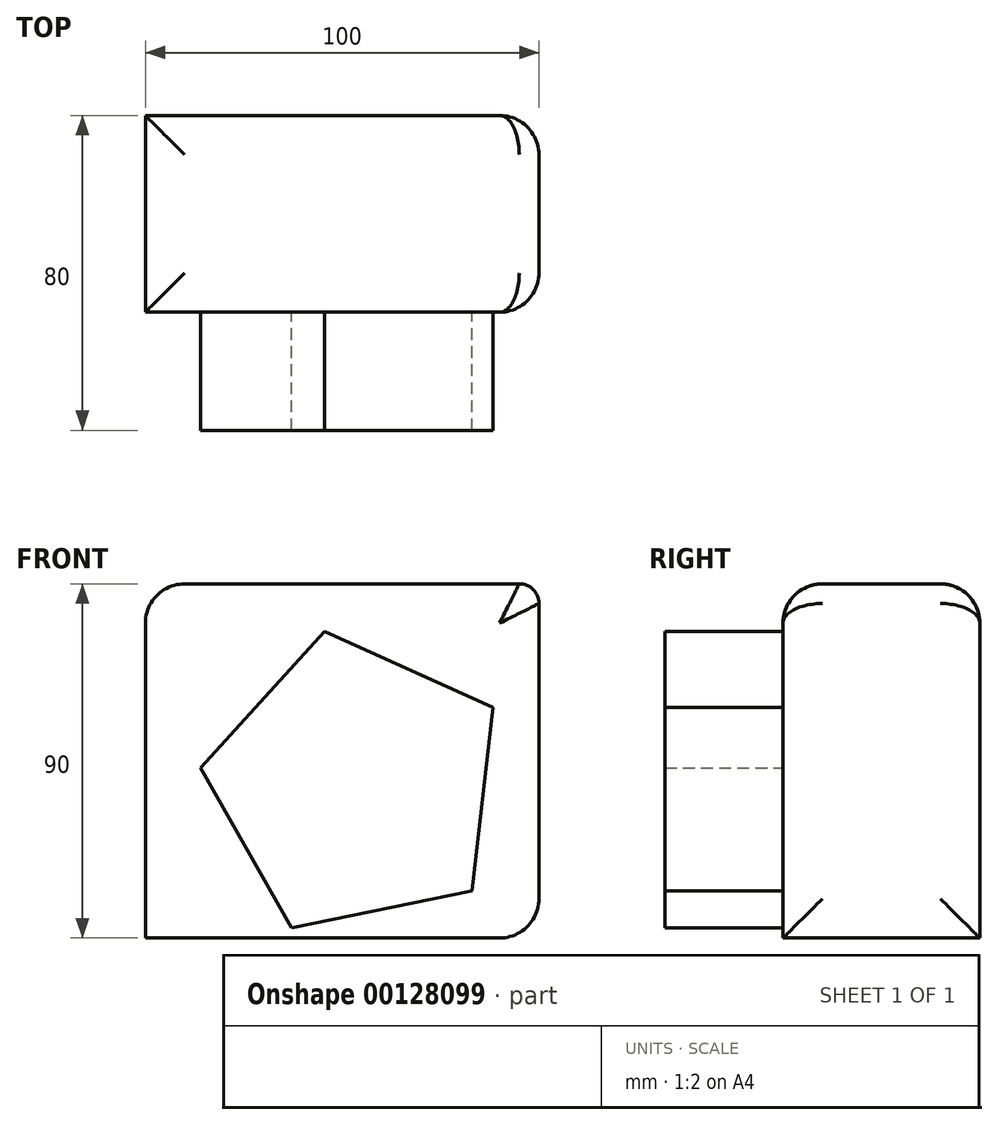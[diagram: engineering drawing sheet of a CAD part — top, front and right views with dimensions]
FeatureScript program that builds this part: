
annotation { "Feature Type Name" : "Feature", "Feature Type Description" : "" }
export const myFeature = defineFeature(function(context is Context, id is Id, definition is map)
    precondition{}
    {
        {
            var Q0;
            Q0=qCreatedBy(makeId("Front.planeOp"),FACE);
            var sketch = newSketch(context, id + "F0", { "sketchPlane" : qUnion([Q0])});
            skLineSegment(sketch, "E0.bottom", {"start": v(-53.61, 60) * mm, "end": v(46.39, 60) * mm});
            skLineSegment(sketch, "E0.top", {"start": v(-53.61, 10) * mm, "end": v(46.39, 10) * mm});
            skLineSegment(sketch, "E0.left", {"start": v(-53.61, 60) * mm, "end": v(-53.61, 10) * mm});
            skLineSegment(sketch, "E0.right", {"start": v(46.39, 60) * mm, "end": v(46.39, 10) * mm});
            skSolve(sketch);
        }
        {
            var Q0;
            Q0=makeQuery(id+"F0.imprint","IMPRINT",FACE,{"disambiguationData":[TD([[makeQuery(id+"F0.imprint","IMPRINT",EDGE,{"derivedFrom":sQuery(id+"F0.wireOp",EDGE,"E0.bottom")}),-1.0]])]});
            extrude(context, id + "F1", {"entities" : qUnion([Q0]), "depth" : 50 * mm});
        }
        {
            var Q0;
            Q0=makeQuery(id+"F1.opExtrude","SWEPT_FACE",FACE,{"disambiguationData":[OSD([sQuery(id+"F0.wireOp",EDGE,"E0.bottom")])]});
            extrude(context, id + "F2", {"entities" : qUnion([Q0]), "operationType" : NewBodyOperationType.ADD, "depth" : 40 * mm});
        }
        {
            var Q0;
            {var subQ0=sQuery(id+"F0.wireOp",EDGE,"E0.bottom");Q0=makeQuery(id+"F2.boolean.opBoolean","MERGE",FACE,{"derivedFrom":[makeQuery(id+"F1.opExtrude","CAP_FACE",FACE,{"disambiguationData":[OSD([subQ0,sQuery(id+"F0.wireOp",EDGE,"E0.top"),sQuery(id+"F0.wireOp",EDGE,"E0.left"),sQuery(id+"F0.wireOp",EDGE,"E0.right")])],"isStart":false}),makeQuery(id+"F2.opExtrude","SWEPT_FACE",FACE,{"disambiguationData":[OSD([subQ0]),TDD([makeQuery(id+"F1.opExtrude","CAP_EDGE",EDGE,{"disambiguationData":[OSD([subQ0])],"isStart":false})])]})]});}
            var sketch = newSketch(context, id + "F3", { "sketchPlane" : qUnion([Q0])});
            skCircle(sketch, "E1", {"center": v(0, 50.07) * mm, "radius": 18.87 * mm});
            skSolve(sketch);
        }
        {
            var Q0;
            Q0=makeQuery(id+"F3.imprint","IMPRINT",FACE,{"disambiguationData":[TD([[makeQuery(id+"F3.imprint","IMPRINT",EDGE,{"derivedFrom":sQuery(id+"F3.wireOp",EDGE,"E1")}),-1.0]])]});
            var sketch = newSketch(context, id + "F4", { "sketchPlane" : qUnion([Q0])});
            skCircle(sketch, "E2.cCircle", {"center": v(0, 48.86) * mm, "radius": 32.25 * mm, "construction": true});
            skLineSegment(sketch, "E2.0", {"start": v(-39.62, 53.29) * mm, "end": v(-8.03, 87.9) * mm});
            skLineSegment(sketch, "E2.1", {"start": v(-8.03, 87.9) * mm, "end": v(34.65, 68.56) * mm});
            skLineSegment(sketch, "E2.2", {"start": v(34.65, 68.56) * mm, "end": v(29.45, 21.99) * mm});
            skLineSegment(sketch, "E2.3", {"start": v(29.45, 21.99) * mm, "end": v(-16.45, 12.55) * mm});
            skLineSegment(sketch, "E2.4", {"start": v(-16.45, 12.55) * mm, "end": v(-39.62, 53.29) * mm});
            skPoint(sketch, "E2.0.midPoint", {"position": v(-23.82, 70.6) * mm});
            skSolve(sketch);
        }
        {
            var Q0;
            Q0 = qSketchRegion(id + "F4", true);
            extrude(context, id + "F5", {"entities" : qUnion([Q0]), "operationType" : NewBodyOperationType.ADD, "depth" : 30 * mm});
        }
        {
            var Q0;
            Q0=makeQuery(id+"F2.opExtrude","CAP_EDGE",EDGE,{"disambiguationData":[OSD([sQuery(id+"F0.wireOp",EDGE,"E0.bottom"),sQuery(id+"F0.wireOp",EDGE,"E0.right")])],"isStart":false});
            fillet(context, id + "F6", {"entities" : qUnion([Q0]), "radius" : 5 * mm, "tangentPropagation" : true, "allowEdgeOverflow" : false});
        }
        {
            var Q0;
            Q0=makeQuery(id+"F2.opExtrude","CAP_FACE",FACE,{"disambiguationData":[OSD([sQuery(id+"F0.wireOp",EDGE,"E0.bottom")])],"isStart":false});
            var Q1;
            {var subQ0=sQuery(id+"F0.wireOp",EDGE,"E0.right");Q1=makeQuery(id+"F2.boolean.opBoolean","MERGE",FACE,{"derivedFrom":[makeQuery(id+"F1.opExtrude","SWEPT_FACE",FACE,{"disambiguationData":[OSD([subQ0])]}),makeQuery(id+"F2.opExtrude","SWEPT_FACE",FACE,{"disambiguationData":[OSD([sQuery(id+"F0.wireOp",EDGE,"E0.bottom"),subQ0])]})]});}
            fillet(context, id + "F7", {"entities" : qUnion([Q0, Q1]), "radius" : 10 * mm, "tangentPropagation" : true, "allowEdgeOverflow" : false});
        }
    });
